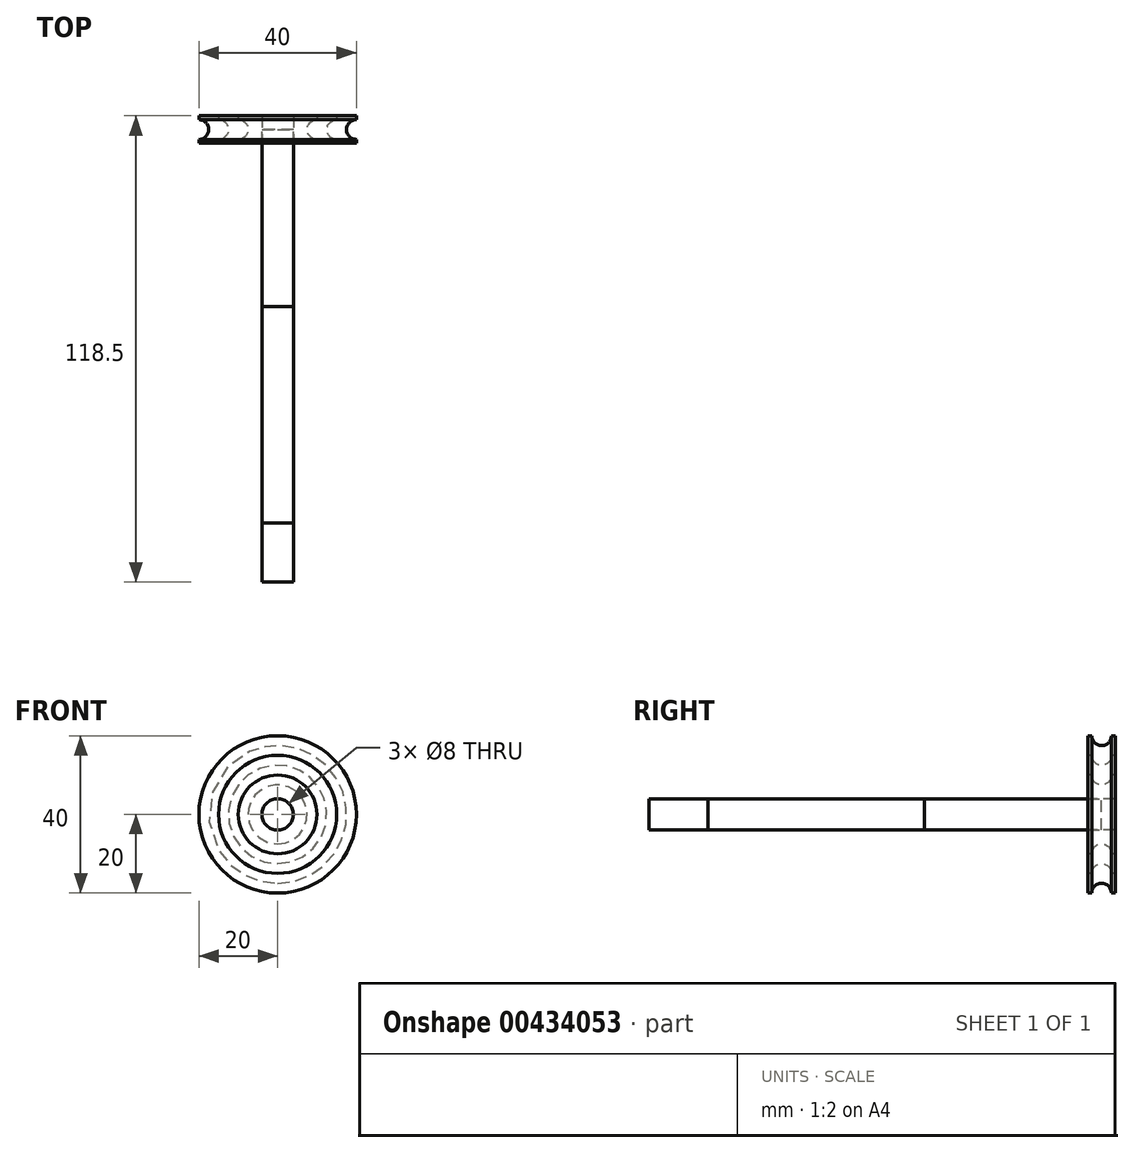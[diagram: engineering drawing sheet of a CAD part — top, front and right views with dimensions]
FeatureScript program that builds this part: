
annotation { "Feature Type Name" : "Feature", "Feature Type Description" : "" }
export const myFeature = defineFeature(function(context is Context, id is Id, definition is map)
    precondition{}
    {
        {
            var Q0;
            Q0=qCreatedBy(makeId("Right.planeOp"),FACE);
            var sketch = newSketch(context, id + "F0", { "sketchPlane" : qUnion([Q0])});
            skLineSegment(sketch, "E0", {"start": v(0, 20) * mm, "end": v(0, -20) * mm, "construction": true});
            skLineSegment(sketch, "E1", {"start": v(-3.5, 20) * mm, "end": v(-3.5, 0) * mm});
            skLineSegment(sketch, "E2", {"start": v(-3.5, 0) * mm, "end": v(3.5, 0) * mm, "construction": true});
            skLineSegment(sketch, "E3", {"start": v(3.5, 0) * mm, "end": v(3.5, 20) * mm});
            skLineSegment(sketch, "E4", {"start": v(-3.5, 20) * mm, "end": v(-2.5, 20) * mm});
            skLineSegment(sketch, "E5", {"start": v(3.5, 20) * mm, "end": v(2.5, 20) * mm});
            skArc(sketch, "E6", {"start": v(-2.5, 20) * mm, "mid": v(0, 17.5) * mm, "end": v(2.5, 20) * mm});
            skLineSegment(sketch, "E7", {"start": v(-3.5, 4) * mm, "end": v(3.5, 4) * mm});
            skSolve(sketch);
        }
        {
            var Q0;
            Q0 = qSketchRegion(id + "F0", true);
            var Q1;
            Q1=sQuery(id+"F0.wireOp",EDGE,"E2");
            revolve(context, id + "F1", {"entities" : qUnion([Q0]), "axis" : qUnion([Q1]), "revolveType" : RevolveType.FULL});
        }
        {
            var Q0;
            Q0=qCreatedBy(makeId("Right.planeOp"),FACE);
            var sketch = newSketch(context, id + "F2", { "sketchPlane" : qUnion([Q0])});
            skLineSegment(sketch, "E8", {"start": v(0, 15) * mm, "end": v(0, -15) * mm, "construction": true});
            skLineSegment(sketch, "E9", {"start": v(-3.5, 15) * mm, "end": v(-3.5, 0) * mm});
            skLineSegment(sketch, "E10", {"start": v(-3.5, 0) * mm, "end": v(3.5, 0) * mm, "construction": true});
            skLineSegment(sketch, "E11", {"start": v(3.5, 0) * mm, "end": v(3.5, 15) * mm});
            skLineSegment(sketch, "E12", {"start": v(-3.5, 15) * mm, "end": v(-2.5, 15) * mm});
            skLineSegment(sketch, "E13", {"start": v(3.5, 15) * mm, "end": v(2.5, 15) * mm});
            skArc(sketch, "E14", {"start": v(-2.5, 15) * mm, "mid": v(0, 12.5) * mm, "end": v(2.5, 15) * mm});
            skLineSegment(sketch, "E15", {"start": v(-3.5, 4) * mm, "end": v(3.5, 4) * mm});
            skSolve(sketch);
        }
        {
            var Q0;
            Q0 = qSketchRegion(id + "F2", true);
            var Q1;
            Q1=sQuery(id+"F2.wireOp",EDGE,"E10");
            revolve(context, id + "F3", {"entities" : qUnion([Q0]), "axis" : qUnion([Q1]), "revolveType" : RevolveType.FULL});
        }
        {
            var Q0;
            Q0=qCreatedBy(makeId("Right.planeOp"),FACE);
            var sketch = newSketch(context, id + "F4", { "sketchPlane" : qUnion([Q0])});
            skLineSegment(sketch, "E16", {"start": v(0, 10) * mm, "end": v(0, -10) * mm, "construction": true});
            skLineSegment(sketch, "E17", {"start": v(-3.5, 10) * mm, "end": v(-3.5, 0) * mm});
            skLineSegment(sketch, "E18", {"start": v(-3.5, 0) * mm, "end": v(3.5, 0) * mm, "construction": true});
            skLineSegment(sketch, "E19", {"start": v(3.5, 0) * mm, "end": v(3.5, 10) * mm});
            skLineSegment(sketch, "E20", {"start": v(-3.5, 10) * mm, "end": v(-2.5, 10) * mm});
            skLineSegment(sketch, "E21", {"start": v(3.5, 10) * mm, "end": v(2.5, 10) * mm});
            skArc(sketch, "E22", {"start": v(-2.5, 10) * mm, "mid": v(0, 7.5) * mm, "end": v(2.5, 10) * mm});
            skLineSegment(sketch, "E23", {"start": v(-3.5, 4) * mm, "end": v(3.5, 4) * mm});
            skSolve(sketch);
        }
        {
            var Q0;
            Q0 = qSketchRegion(id + "F4", true);
            var Q1;
            Q1=sQuery(id+"F4.wireOp",EDGE,"E18");
            revolve(context, id + "F5", {"entities" : qUnion([Q0]), "axis" : qUnion([Q1]), "revolveType" : RevolveType.FULL});
        }
        {
            var Q0;
            Q0=qCreatedBy(makeId("Front.planeOp"),FACE);
            var sketch = newSketch(context, id + "F6", { "sketchPlane" : qUnion([Q0])});
            skCircle(sketch, "E24.0", {"center": v(0, 0) * mm, "radius": 4 * mm});
            skSolve(sketch);
        }
        {
            var Q0;
            Q0 = qSketchRegion(id + "F6", true);
            extrude(context, id + "F7", {"entities" : qUnion([Q0]), "depth" : 45 * mm});
        }
        {
            var Q0;
            Q0=makeQuery(id+"F7.opExtrude","CAP_FACE",FACE,{"disambiguationData":[OSD([sQuery(id+"F6.wireOp",EDGE,"E24.0")])],"isStart":false});
            extrude(context, id + "F8", {"entities" : qUnion([Q0]), "depth" : 55 * mm});
        }
        {
            var Q0;
            Q0=makeQuery(id+"F8.opExtrude","CAP_FACE",FACE,{"disambiguationData":[OSD([sQuery(id+"F6.wireOp",EDGE,"E24.0")])],"isStart":false});
            extrude(context, id + "F9", {"entities" : qUnion([Q0]), "depth" : 15 * mm});
        }
    });
